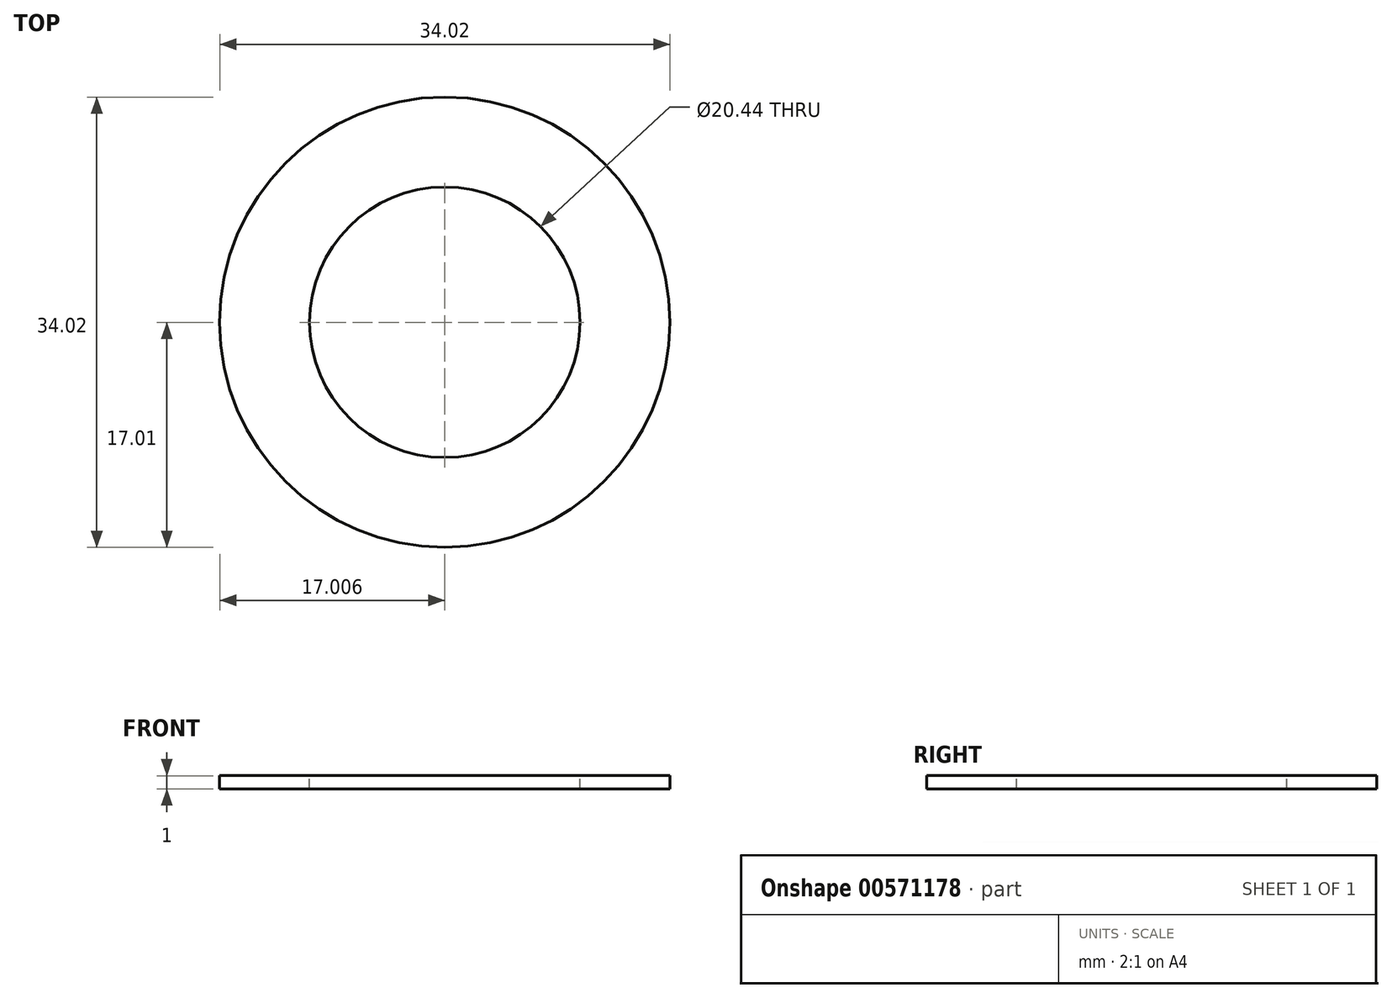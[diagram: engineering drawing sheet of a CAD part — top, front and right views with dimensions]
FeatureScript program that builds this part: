
annotation { "Feature Type Name" : "Feature", "Feature Type Description" : "" }
export const myFeature = defineFeature(function(context is Context, id is Id, definition is map)
    precondition{}
    {
        {
            var Q0;
            Q0=qCreatedBy(makeId("Front.planeOp"),FACE);
            var sketch = newSketch(context, id + "F0", { "sketchPlane" : qUnion([Q0])});
            skLineSegment(sketch, "E0.bottom", {"start": v(-10.41, 3.1) * mm, "end": v(-3.62, 3.1) * mm});
            skLineSegment(sketch, "E0.top", {"start": v(-10.41, 2.1) * mm, "end": v(-3.62, 2.1) * mm});
            skLineSegment(sketch, "E0.left", {"start": v(-10.41, 3.1) * mm, "end": v(-10.41, 2.1) * mm});
            skLineSegment(sketch, "E0.right", {"start": v(-3.62, 3.1) * mm, "end": v(-3.62, 2.1) * mm});
            skLineSegment(sketch, "E1", {"start": v(-20.63, 8.52) * mm, "end": v(-20.63, -2.28) * mm, "construction": true});
            skSolve(sketch);
        }
        {
            var Q0;
            Q0 = qSketchRegion(id + "F0", true);
            var Q1;
            Q1=sQuery(id+"F0.wireOp",EDGE,"E1");
            revolve(context, id + "F1", {"entities" : qUnion([Q0]), "axis" : qUnion([Q1]), "revolveType" : RevolveType.FULL});
        }
    });
